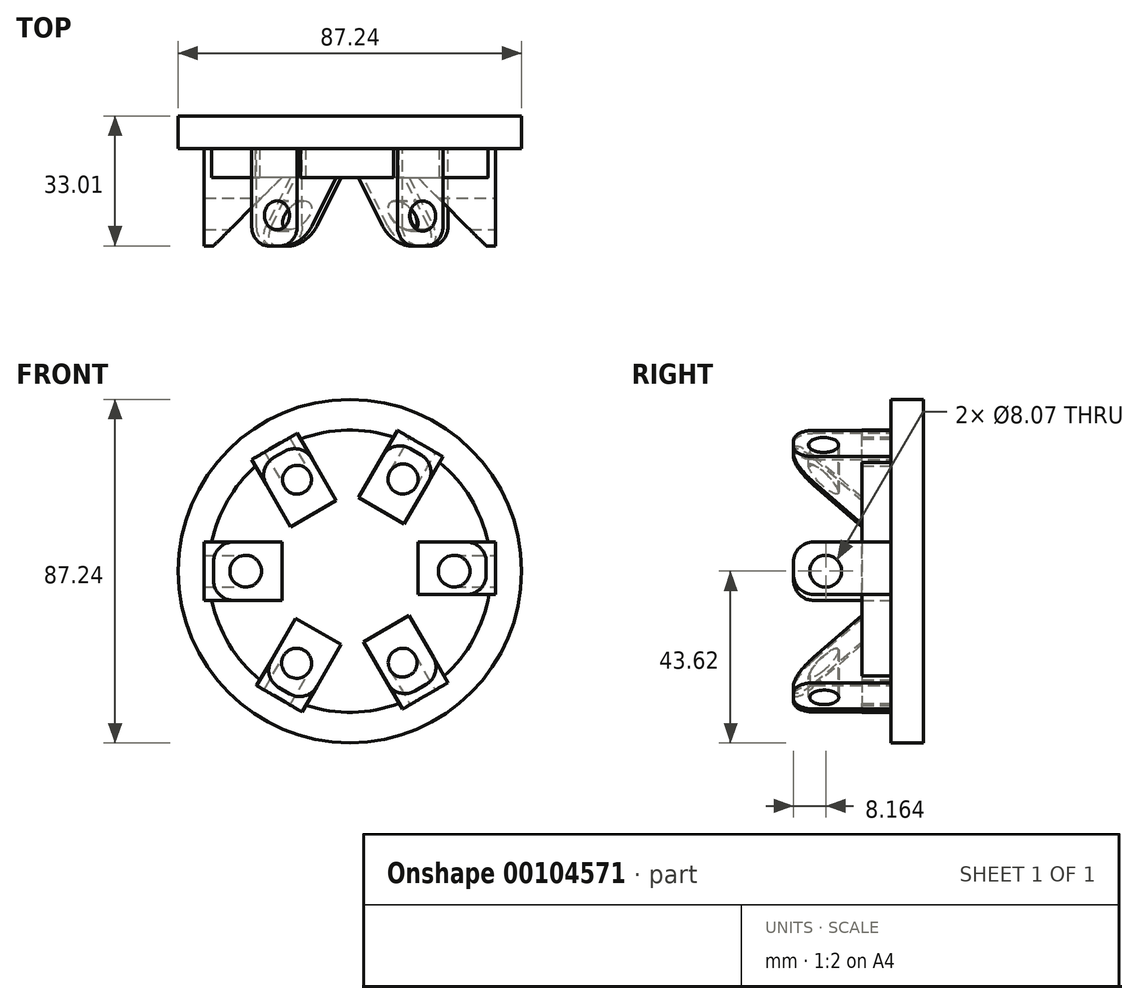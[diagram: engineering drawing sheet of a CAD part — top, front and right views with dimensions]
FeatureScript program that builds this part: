
annotation { "Feature Type Name" : "Feature", "Feature Type Description" : "" }
export const myFeature = defineFeature(function(context is Context, id is Id, definition is map)
    precondition{}
    {
        {
            var Q0;
            Q0=qCreatedBy(makeId("Front.planeOp"),FACE);
            var sketch = newSketch(context, id + "F0", { "sketchPlane" : qUnion([Q0])});
            skCircle(sketch, "E0", {"center": v(0, 0) * mm, "radius": 43.62 * mm});
            skSolve(sketch);
        }
        {
            var Q0;
            Q0 = qSketchRegion(id + "F0", true);
            extrude(context, id + "F1", {"entities" : qUnion([Q0]), "endBound" : BoundingType.SYMMETRIC, "depth" : 8.27 * mm});
        }
        {
            var Q0;
            Q0=makeQuery(id+"F1.opExtrude","CAP_FACE",FACE,{"disambiguationData":[OSD([sQuery(id+"F0.wireOp",EDGE,"E0")])],"isStart":false});
            var sketch = newSketch(context, id + "F2", { "sketchPlane" : qUnion([Q0])});
            skCircle(sketch, "E1", {"center": v(0, 0) * mm, "radius": 35.85 * mm});
            skSolve(sketch);
        }
        {
            var Q0;
            Q0 = qSketchRegion(id + "F2", true);
            extrude(context, id + "F3", {"entities" : qUnion([Q0]), "operationType" : NewBodyOperationType.ADD, "depth" : 7.37 * mm});
        }
        {
            var Q0;
            Q0=qCreatedBy(makeId("Front.planeOp"),FACE);
            var sketch = newSketch(context, id + "F4", { "sketchPlane" : qUnion([Q0])});
            skLineSegment(sketch, "E2", {"start": v(-37.03, 7.42) * mm, "end": v(-37.03, -5.96) * mm});
            skLineSegment(sketch, "E3", {"start": v(-37.03, 7.42) * mm, "end": v(-16.86, 7.42) * mm});
            skLineSegment(sketch, "E4", {"start": v(-16.86, 7.42) * mm, "end": v(-16.86, -5.22) * mm});
            skLineSegment(sketch, "E5", {"start": v(-16.86, -5.96) * mm, "end": v(-16.86, -5.22) * mm});
            skLineSegment(sketch, "E6.MirrorCS", {"start": v(16.86, 7.42) * mm, "end": v(16.86, -5.22) * mm});
            skLineSegment(sketch, "E7.MirrorCS", {"start": v(37.03, 7.42) * mm, "end": v(16.86, 7.42) * mm});
            skLineSegment(sketch, "E8.MirrorCS", {"start": v(37.03, -5.96) * mm, "end": v(16.86, -5.96) * mm});
            skLineSegment(sketch, "E9.MirrorCS", {"start": v(37.03, 7.42) * mm, "end": v(37.03, -5.96) * mm});
            skLineSegment(sketch, "E10.MirrorCS", {"start": v(16.86, -5.96) * mm, "end": v(16.86, -5.22) * mm});
            skLineSegment(sketch, "E11.1.0", {"start": v(14.86, -10.9) * mm, "end": v(3.9, -17.22) * mm});
            skLineSegment(sketch, "E11.1.1", {"start": v(3.27, -17.58) * mm, "end": v(3.9, -17.22) * mm});
            skLineSegment(sketch, "E11.1.2", {"start": v(13.35, -35.04) * mm, "end": v(3.27, -17.58) * mm});
            skLineSegment(sketch, "E11.1.3", {"start": v(24.94, -28.35) * mm, "end": v(14.86, -10.9) * mm});
            skLineSegment(sketch, "E11.1.4", {"start": v(24.94, -28.35) * mm, "end": v(13.35, -35.04) * mm});
            skLineSegment(sketch, "E11.2.0", {"start": v(-2, -18.32) * mm, "end": v(-12.96, -12) * mm});
            skLineSegment(sketch, "E11.2.1", {"start": v(-13.6, -11.63) * mm, "end": v(-12.96, -12) * mm});
            skLineSegment(sketch, "E11.2.2", {"start": v(-23.67, -29.09) * mm, "end": v(-13.6, -11.63) * mm});
            skLineSegment(sketch, "E11.2.3", {"start": v(-12.08, -35.78) * mm, "end": v(-2, -18.32) * mm});
            skLineSegment(sketch, "E11.2.4", {"start": v(-12.08, -35.78) * mm, "end": v(-23.67, -29.09) * mm});
            skLineSegment(sketch, "E11.3.0", {"start": v(-16.86, -7.42) * mm, "end": v(-16.86, 5.22) * mm});
            skLineSegment(sketch, "E11.3.1", {"start": v(-16.86, 5.96) * mm, "end": v(-16.86, 5.22) * mm});
            skLineSegment(sketch, "E11.3.3", {"start": v(-37.03, -7.42) * mm, "end": v(-16.86, -7.42) * mm});
            skLineSegment(sketch, "E11.3.4", {"start": v(-37.03, -7.42) * mm, "end": v(-37.03, 5.96) * mm});
            skLineSegment(sketch, "E11.4.0", {"start": v(-14.86, 10.9) * mm, "end": v(-3.9, 17.22) * mm});
            skLineSegment(sketch, "E11.4.1", {"start": v(-3.27, 17.58) * mm, "end": v(-3.9, 17.22) * mm});
            skLineSegment(sketch, "E11.4.2", {"start": v(-13.35, 35.04) * mm, "end": v(-3.27, 17.58) * mm});
            skLineSegment(sketch, "E11.4.3", {"start": v(-24.94, 28.35) * mm, "end": v(-14.86, 10.9) * mm});
            skLineSegment(sketch, "E11.4.4", {"start": v(-24.94, 28.35) * mm, "end": v(-13.35, 35.04) * mm});
            skLineSegment(sketch, "E11.5.0", {"start": v(2, 18.32) * mm, "end": v(12.96, 12) * mm});
            skLineSegment(sketch, "E11.5.1", {"start": v(13.6, 11.63) * mm, "end": v(12.96, 12) * mm});
            skLineSegment(sketch, "E11.5.2", {"start": v(23.67, 29.09) * mm, "end": v(13.6, 11.63) * mm});
            skLineSegment(sketch, "E11.5.3", {"start": v(12.08, 35.78) * mm, "end": v(2, 18.32) * mm});
            skLineSegment(sketch, "E11.5.4", {"start": v(12.08, 35.78) * mm, "end": v(23.67, 29.09) * mm});
            skPoint(sketch, "E11.center", {"position": v(0, 0) * mm});
            skLineSegment(sketch, "E11.anchor1", {"start": v(0, 0) * mm, "end": v(16.86, -5.22) * mm, "construction": true});
            skLineSegment(sketch, "E11.anchor2", {"start": v(0, 0) * mm, "end": v(12.96, 12) * mm, "construction": true});
            skSolve(sketch);
        }
        {
            var Q0;
            Q0 = qSketchRegion(id + "F4", true);
            extrude(context, id + "F5", {"entities" : qUnion([Q0]), "operationType" : NewBodyOperationType.ADD, "depth" : 28.72 * mm});
        }
        {
            var Q0;
            Q0=makeQuery(id+"F5.opExtrude","CAP_EDGE",EDGE,{"disambiguationData":[OSD([sQuery(id+"F4.wireOp",EDGE,"E4"),sQuery(id+"F4.wireOp",EDGE,"E5")])],"isStart":false});
            chamfer(context, id + "F6", {"entities" : qUnion([Q0]), "width" : 17.78 * mm, "tangentPropagation" : true});
        }
        {
            var Q0;
            Q0=makeQuery(id+"F5.opExtrude","CAP_EDGE",EDGE,{"disambiguationData":[OSD([sQuery(id+"F4.wireOp",EDGE,"E6.MirrorCS"),sQuery(id+"F4.wireOp",EDGE,"E10.MirrorCS")])],"isStart":false});
            chamfer(context, id + "F7", {"entities" : qUnion([Q0]), "width" : 17.78 * mm, "tangentPropagation" : true});
        }
        {
            var Q0;
            Q0 = qSketchRegion(id + "F4", true);
            extrude(context, id + "F8", {"entities" : qUnion([Q0]), "operationType" : NewBodyOperationType.ADD, "depth" : 28.88 * mm});
        }
        {
            var Q0;
            Q0=makeQuery(id+"F8.opExtrude","CAP_EDGE",EDGE,{"disambiguationData":[OSD([sQuery(id+"F4.wireOp",EDGE,"E11.5.0"),sQuery(id+"F4.wireOp",EDGE,"E11.5.1")])],"isStart":false});
            var Q1;
            Q1=makeQuery(id+"F8.opExtrude","CAP_EDGE",EDGE,{"disambiguationData":[OSD([sQuery(id+"F4.wireOp",EDGE,"E11.4.0"),sQuery(id+"F4.wireOp",EDGE,"E11.4.1")])],"isStart":false});
            var Q2;
            Q2=makeQuery(id+"F8.opExtrude","CAP_EDGE",EDGE,{"disambiguationData":[OSD([sQuery(id+"F4.wireOp",EDGE,"E4"),sQuery(id+"F4.wireOp",EDGE,"E11.3.0"),sQuery(id+"F4.wireOp",EDGE,"E11.3.1")])],"isStart":false});
            var Q3;
            Q3=makeQuery(id+"F8.opExtrude","CAP_EDGE",EDGE,{"disambiguationData":[OSD([sQuery(id+"F4.wireOp",EDGE,"E11.2.0"),sQuery(id+"F4.wireOp",EDGE,"E11.2.1")])],"isStart":false});
            var Q4;
            Q4=makeQuery(id+"F8.opExtrude","CAP_EDGE",EDGE,{"disambiguationData":[OSD([sQuery(id+"F4.wireOp",EDGE,"E11.1.0"),sQuery(id+"F4.wireOp",EDGE,"E11.1.1")])],"isStart":false});
            var Q5;
            Q5=makeQuery(id+"F8.opExtrude","CAP_EDGE",EDGE,{"disambiguationData":[OSD([sQuery(id+"F4.wireOp",EDGE,"E6.MirrorCS"),sQuery(id+"F4.wireOp",EDGE,"E10.MirrorCS")])],"isStart":false});
            chamfer(context, id + "F9", {"entities" : qUnion([Q0, Q1, Q2, Q3, Q4, Q5]), "width" : 17.78 * mm, "tangentPropagation" : true});
        }
        {
            var Q0;
            Q0=makeQuery(id+"F8.opExtrude","CAP_EDGE",EDGE,{"disambiguationData":[OSD([sQuery(id+"F4.wireOp",EDGE,"E11.1.2")])],"isStart":false});
            var Q1;
            Q1=makeQuery(id+"F8.opExtrude","CAP_EDGE",EDGE,{"disambiguationData":[OSD([sQuery(id+"F4.wireOp",EDGE,"E11.1.3")])],"isStart":false});
            var Q2;
            Q2=makeQuery(id+"F8.opExtrude","CAP_EDGE",EDGE,{"disambiguationData":[OSD([sQuery(id+"F4.wireOp",EDGE,"E11.2.3")])],"isStart":false});
            var Q3;
            Q3=makeQuery(id+"F8.opExtrude","CAP_EDGE",EDGE,{"disambiguationData":[OSD([sQuery(id+"F4.wireOp",EDGE,"E11.2.2")])],"isStart":false});
            var Q4;
            Q4=makeQuery(id+"F8.opExtrude","CAP_EDGE",EDGE,{"disambiguationData":[OSD([sQuery(id+"F4.wireOp",EDGE,"E11.3.3")])],"isStart":false});
            var Q5;
            Q5=makeQuery(id+"F8.opExtrude","CAP_EDGE",EDGE,{"disambiguationData":[OSD([sQuery(id+"F4.wireOp",EDGE,"E3")])],"isStart":false});
            var Q6;
            Q6=makeQuery(id+"F8.opExtrude","CAP_EDGE",EDGE,{"disambiguationData":[OSD([sQuery(id+"F4.wireOp",EDGE,"E7.MirrorCS")])],"isStart":false});
            var Q7;
            Q7=makeQuery(id+"F8.opExtrude","CAP_EDGE",EDGE,{"disambiguationData":[OSD([sQuery(id+"F4.wireOp",EDGE,"E8.MirrorCS")])],"isStart":false});
            var Q8;
            Q8=makeQuery(id+"F8.opExtrude","CAP_EDGE",EDGE,{"disambiguationData":[OSD([sQuery(id+"F4.wireOp",EDGE,"E11.5.2")])],"isStart":false});
            var Q9;
            Q9=makeQuery(id+"F8.opExtrude","CAP_EDGE",EDGE,{"disambiguationData":[OSD([sQuery(id+"F4.wireOp",EDGE,"E11.5.3")])],"isStart":false});
            var Q10;
            Q10=makeQuery(id+"F8.opExtrude","CAP_EDGE",EDGE,{"disambiguationData":[OSD([sQuery(id+"F4.wireOp",EDGE,"E11.4.3")])],"isStart":false});
            var Q11;
            Q11=makeQuery(id+"F8.opExtrude","CAP_EDGE",EDGE,{"disambiguationData":[OSD([sQuery(id+"F4.wireOp",EDGE,"E11.4.2")])],"isStart":false});
            fillet(context, id + "F10", {"entities" : qUnion([Q0, Q1, Q2, Q3, Q4, Q5, Q6, Q7, Q8, Q9, Q10, Q11]), "radius" : 5.08 * mm, "tangentPropagation" : true, "allowEdgeOverflow" : false});
        }
        {
            var Q0;
            {var subQ0=sQuery(id+"F4.wireOp",EDGE,"E9.MirrorCS");Q0=makeQuery(id+"F8.boolean.opBoolean","MERGE",FACE,{"derivedFrom":[makeQuery(id+"F5.opExtrude","SWEPT_FACE",FACE,{"disambiguationData":[OSD([subQ0])]}),makeQuery(id+"F8.opExtrude","SWEPT_FACE",FACE,{"disambiguationData":[OSD([subQ0])]})]});}
            var sketch = newSketch(context, id + "F11", { "sketchPlane" : qUnion([Q0])});
            skCircle(sketch, "E12", {"center": v(-20.72, 0) * mm, "radius": 4.03 * mm});
            skSolve(sketch);
        }
        {
            var Q0;
            Q0 = qSketchRegion(id + "F11", true);
            extrude(context, id + "F12", {"entities" : qUnion([Q0]), "operationType" : NewBodyOperationType.REMOVE, "oppositeDirection" : true, "depth" : 87.8 * mm});
        }
        {
            var Q0;
            {var subQ0=sQuery(id+"F4.wireOp",EDGE,"E11.5.4");Q0=makeQuery(id+"F8.boolean.opBoolean","MERGE",FACE,{"derivedFrom":[makeQuery(id+"F5.opExtrude","SWEPT_FACE",FACE,{"disambiguationData":[OSD([subQ0])]}),makeQuery(id+"F8.opExtrude","SWEPT_FACE",FACE,{"disambiguationData":[OSD([subQ0])]})]});}
            var sketch = newSketch(context, id + "F13", { "sketchPlane" : qUnion([Q0])});
            skCircle(sketch, "E13", {"center": v(-1.36, -21.58) * mm, "radius": 3.98 * mm});
            skSolve(sketch);
        }
        {
            var Q0;
            Q0=makeQuery(id+"F13.imprint","IMPRINT",FACE,{"disambiguationData":[TD([[makeQuery(id+"F13.imprint","IMPRINT",EDGE,{"derivedFrom":sQuery(id+"F13.wireOp",EDGE,"E13")}),-1.0]])]});
            var sketch = newSketch(context, id + "F14", { "sketchPlane" : qUnion([Q0])});
            skCircle(sketch, "E14", {"center": v(0, -21.27) * mm, "radius": 3.83 * mm});
            skSolve(sketch);
        }
        {
            var Q0;
            Q0 = qSketchRegion(id + "F14", true);
            extrude(context, id + "F15", {"entities" : qUnion([Q0]), "operationType" : NewBodyOperationType.REMOVE, "oppositeDirection" : true, "depth" : 90.2 * mm});
        }
        {
            var Q0;
            {var subQ0=sQuery(id+"F4.wireOp",EDGE,"E11.1.4");Q0=makeQuery(id+"F8.boolean.opBoolean","MERGE",FACE,{"derivedFrom":[makeQuery(id+"F5.opExtrude","SWEPT_FACE",FACE,{"disambiguationData":[OSD([subQ0])]}),makeQuery(id+"F8.opExtrude","SWEPT_FACE",FACE,{"disambiguationData":[OSD([subQ0])]})]});}
            var sketch = newSketch(context, id + "F16", { "sketchPlane" : qUnion([Q0])});
            skCircle(sketch, "E15", {"center": v(0.97, 20.72) * mm, "radius": 3.77 * mm});
            skSolve(sketch);
        }
        {
            var Q0;
            Q0=makeQuery(id+"F16.imprint","IMPRINT",FACE,{"disambiguationData":[TD([[makeQuery(id+"F16.imprint","IMPRINT",EDGE,{"derivedFrom":sQuery(id+"F16.wireOp",EDGE,"E15")}),1.0]])]});
            var sketch = newSketch(context, id + "F17", { "sketchPlane" : qUnion([Q0])});
            skCircle(sketch, "E16", {"center": v(0, 21.08) * mm, "radius": 3.68 * mm});
            skSolve(sketch);
        }
        {
            var Q0;
            Q0 = qSketchRegion(id + "F17", true);
            extrude(context, id + "F18", {"entities" : qUnion([Q0]), "operationType" : NewBodyOperationType.REMOVE, "oppositeDirection" : true, "depth" : 79.12 * mm});
        }
    });
